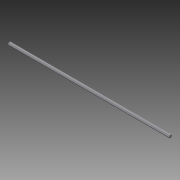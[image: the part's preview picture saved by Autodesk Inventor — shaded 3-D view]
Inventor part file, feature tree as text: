
AUTODESK INVENTOR PART (.ipt)
format: ipt  version: 2015 SP1 (Build 190203100, 203)  size: 77,824 bytes
history: native  units: in
note: dims shown in document units (in); Inventor stores cm internally (conversion verified against a paired STEP export)
features: extrude x1, sketch x1
ambient origin geometry x8: Origin, YZ Plane, XZ Plane, XY Plane, X Axis, Y Axis, Z Axis, Center Point
bodies: Solid1 (feature_tree)
feature tree (2):
  extrude  "Extrusion1"  Depth=0.4375in
  sketch  "Sketch1"  dims[d0=0.4375in d1=0.4375in d2=0.4375in d3=0.2188in d4=120.0deg d5=120.0deg d6=0.2188in d7=0.2188in d8=27.0in d9=0.0in]
